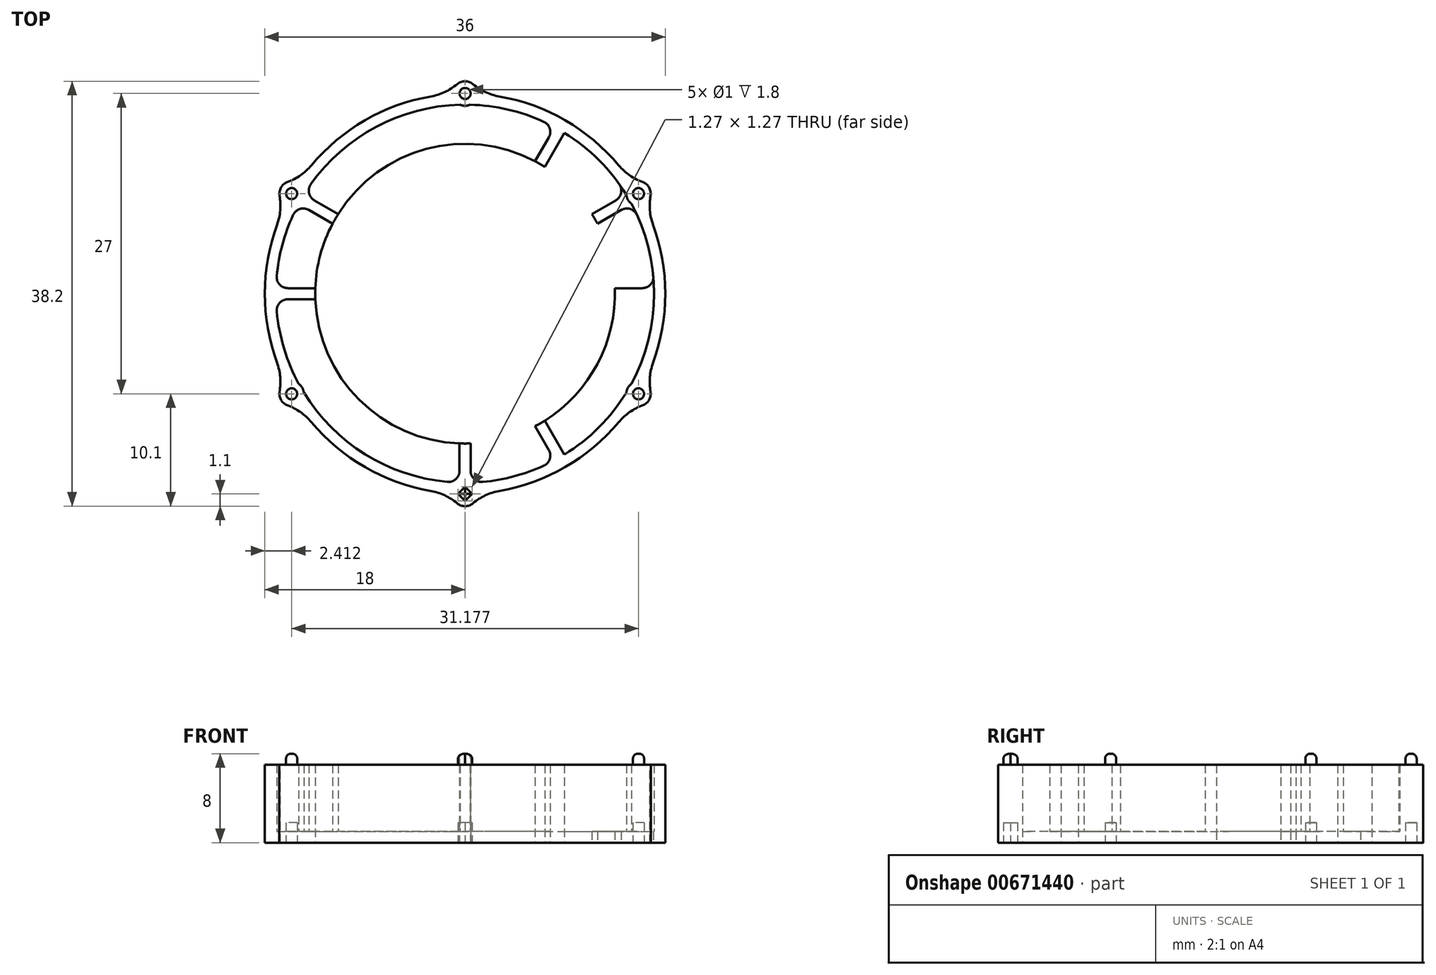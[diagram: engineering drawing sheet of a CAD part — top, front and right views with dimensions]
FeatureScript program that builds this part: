
annotation { "Feature Type Name" : "Feature", "Feature Type Description" : "" }
export const myFeature = defineFeature(function(context is Context, id is Id, definition is map)
    precondition{}
    {
        {
            var Q0;
            Q0=qCreatedBy(makeId("Top.planeOp"),FACE);
            var sketch = newSketch(context, id + "F0", { "sketchPlane" : qUnion([Q0])});
            skCircle(sketch, "E0", {"center": v(0, 0) * mm, "radius": 18 * mm});
            skCircle(sketch, "E1.0", {"center": v(0, 0) * mm, "radius": 17 * mm});
            skLineSegment(sketch, "E2.bottom", {"start": v(8.56, 15.83) * mm, "end": v(9.43, 15.33) * mm});
            skLineSegment(sketch, "E2.top", {"start": v(-9.43, -15.33) * mm, "end": v(-8.56, -15.83) * mm});
            skLineSegment(sketch, "E2.left", {"start": v(8.56, 15.83) * mm, "end": v(-9.43, -15.33) * mm});
            skLineSegment(sketch, "E2.right", {"start": v(9.43, 15.33) * mm, "end": v(-8.56, -15.83) * mm});
            skLineSegment(sketch, "E3.bottom", {"start": v(15.33, 9.43) * mm, "end": v(15.83, 8.56) * mm});
            skLineSegment(sketch, "E3.top", {"start": v(-15.83, -8.56) * mm, "end": v(-15.33, -9.43) * mm});
            skLineSegment(sketch, "E3.left", {"start": v(15.33, 9.43) * mm, "end": v(-15.83, -8.56) * mm});
            skLineSegment(sketch, "E3.right", {"start": v(15.83, 8.56) * mm, "end": v(-15.33, -9.43) * mm});
            skLineSegment(sketch, "E4", {"start": v(-38.35, 0) * mm, "end": v(39.17, 0) * mm, "construction": true});
            skLineSegment(sketch, "E5", {"start": v(0, 42.5) * mm, "end": v(0, -42.47) * mm, "construction": true});
            skLineSegment(sketch, "E6.bottom", {"start": v(-18, 0.5) * mm, "end": v(18, 0.5) * mm});
            skLineSegment(sketch, "E6.top", {"start": v(-18, -0.5) * mm, "end": v(18, -0.5) * mm});
            skLineSegment(sketch, "E6.left", {"start": v(-18, 0.5) * mm, "end": v(-18, -0.5) * mm});
            skLineSegment(sketch, "E6.right", {"start": v(18, 0.5) * mm, "end": v(18, -0.5) * mm});
            skLineSegment(sketch, "E7.bottom", {"start": v(-15.33, 9.43) * mm, "end": v(15.83, -8.56) * mm});
            skLineSegment(sketch, "E7.top", {"start": v(-15.83, 8.56) * mm, "end": v(15.33, -9.43) * mm});
            skLineSegment(sketch, "E7.left", {"start": v(-15.33, 9.43) * mm, "end": v(-15.83, 8.56) * mm});
            skLineSegment(sketch, "E7.right", {"start": v(15.83, -8.56) * mm, "end": v(15.33, -9.43) * mm});
            skLineSegment(sketch, "E8.bottom", {"start": v(-0.5, 18) * mm, "end": v(0.5, 18) * mm});
            skLineSegment(sketch, "E8.top", {"start": v(-0.5, -18) * mm, "end": v(0.5, -18) * mm});
            skLineSegment(sketch, "E8.left", {"start": v(-0.5, 18) * mm, "end": v(-0.5, -18) * mm});
            skLineSegment(sketch, "E8.right", {"start": v(0.5, 18) * mm, "end": v(0.5, -18) * mm});
            skLineSegment(sketch, "E9.bottom", {"start": v(-9.43, 15.33) * mm, "end": v(-8.56, 15.83) * mm});
            skLineSegment(sketch, "E9.top", {"start": v(8.56, -15.83) * mm, "end": v(9.43, -15.33) * mm});
            skLineSegment(sketch, "E9.left", {"start": v(-9.43, 15.33) * mm, "end": v(8.56, -15.83) * mm});
            skLineSegment(sketch, "E9.right", {"start": v(-8.56, 15.83) * mm, "end": v(9.43, -15.33) * mm});
            skCircle(sketch, "E10", {"center": v(0, 0) * mm, "radius": 13.47 * mm});
            skSolve(sketch);
        }
        {
            var Q0;
            Q0=qCreatedBy(makeId("Top.planeOp"),FACE);
            var sketch = newSketch(context, id + "F1", { "sketchPlane" : qUnion([Q0])});
            skCircle(sketch, "E11", {"center": v(0, 0) * mm, "radius": 18 * mm});
            skCircle(sketch, "E12", {"center": v(0, 0) * mm, "radius": 17 * mm});
            skSolve(sketch);
        }
        {
            var Q0;
            Q0=makeQuery(id+"F1.imprint","IMPRINT",FACE,{"disambiguationData":[TD([[makeQuery(id+"F1.imprint","IMPRINT",EDGE,{"derivedFrom":sQuery(id+"F1.wireOp",EDGE,"E11")}),1.0]])]});
            extrude(context, id + "F2", {"entities" : qUnion([Q0]), "depth" : 7 * mm, "offsetDistance" : 25 * mm});
        }
        {
            var Q0;
            {var subQ0=sQuery(id+"F0.wireOp",EDGE,"E7.bottom");var subQ1=sQuery(id+"F0.wireOp",EDGE,"E1.0");var subQ2=makeQuery(id+"F0.imprint","INTERSECT",VERTEX,{"disambiguationData":[OD(0.0)],"derivedFrom":[subQ1,subQ0]});Q0=makeQuery(id+"F0.imprint","IMPRINT",FACE,{"disambiguationData":[TD([[makeQuery(id+"F0.imprint","IMPRINT",EDGE,{"disambiguationData":[TD([[subQ2,-1.0]])],"derivedFrom":subQ1}),1.0]])]});}
            var Q1;
            {var subQ0=sQuery(id+"F0.wireOp",EDGE,"E2.right");var subQ1=sQuery(id+"F0.wireOp",EDGE,"E1.0");var subQ2=makeQuery(id+"F0.imprint","INTERSECT",VERTEX,{"disambiguationData":[OD(0.0)],"derivedFrom":[subQ1,subQ0]});Q1=makeQuery(id+"F0.imprint","IMPRINT",FACE,{"disambiguationData":[TD([[makeQuery(id+"F0.imprint","IMPRINT",EDGE,{"disambiguationData":[TD([[subQ2,-1.0]])],"derivedFrom":subQ1}),1.0]])]});}
            var Q2;
            {var subQ0=sQuery(id+"F0.wireOp",EDGE,"E8.left");var subQ1=sQuery(id+"F0.wireOp",EDGE,"E1.0");var subQ2=makeQuery(id+"F0.imprint","INTERSECT",VERTEX,{"disambiguationData":[OD(1.0)],"derivedFrom":[subQ1,subQ0]});Q2=makeQuery(id+"F0.imprint","IMPRINT",FACE,{"disambiguationData":[TD([[makeQuery(id+"F0.imprint","IMPRINT",EDGE,{"disambiguationData":[TD([[subQ2,-1.0]])],"derivedFrom":subQ1}),1.0]])]});}
            var Q3;
            {var subQ0=sQuery(id+"F0.wireOp",EDGE,"E9.left");var subQ1=sQuery(id+"F0.wireOp",EDGE,"E1.0");var subQ2=makeQuery(id+"F0.imprint","INTERSECT",VERTEX,{"disambiguationData":[OD(1.0)],"derivedFrom":[subQ1,subQ0]});Q3=makeQuery(id+"F0.imprint","IMPRINT",FACE,{"disambiguationData":[TD([[makeQuery(id+"F0.imprint","IMPRINT",EDGE,{"disambiguationData":[TD([[subQ2,-1.0]])],"derivedFrom":subQ1}),1.0]])]});}
            var Q4;
            {var subQ0=sQuery(id+"F0.wireOp",EDGE,"E6.bottom");var subQ1=sQuery(id+"F0.wireOp",EDGE,"E1.0");var subQ2=makeQuery(id+"F0.imprint","INTERSECT",VERTEX,{"disambiguationData":[OD(1.0)],"derivedFrom":[subQ1,subQ0]});Q4=makeQuery(id+"F0.imprint","IMPRINT",FACE,{"disambiguationData":[TD([[makeQuery(id+"F0.imprint","IMPRINT",EDGE,{"disambiguationData":[TD([[subQ2,-1.0]])],"derivedFrom":subQ1}),1.0]])]});}
            extrude(context, id + "F3", {"entities" : qUnion([Q0, Q1, Q2, Q3, Q4]), "operationType" : NewBodyOperationType.ADD, "depth" : 7 * mm, "offsetDistance" : 25 * mm});
        }
        {
            var Q0;
            Q0=makeQuery(id+"F1.imprint","IMPRINT",FACE,{"disambiguationData":[TD([[makeQuery(id+"F1.imprint","IMPRINT",EDGE,{"derivedFrom":sQuery(id+"F1.wireOp",EDGE,"E11")}),1.0]])]});
            var Q1;
            Q1=makeQuery(id+"F1.imprint","IMPRINT",FACE,{"disambiguationData":[TD([[makeQuery(id+"F1.imprint","IMPRINT",EDGE,{"derivedFrom":sQuery(id+"F1.wireOp",EDGE,"E12")}),1.0]])]});
            extrude(context, id + "F4", {"entities" : qUnion([Q0, Q1]), "operationType" : NewBodyOperationType.ADD, "depth" : 1 * mm, "offsetDistance" : 25 * mm});
        }
        {
            var Q0;
            Q0=qCreatedBy(makeId("Top.planeOp"),FACE);
            var sketch = newSketch(context, id + "F5", { "sketchPlane" : qUnion([Q0])});
            skCircle(sketch, "E13", {"center": v(0, 0) * mm, "radius": 18 * mm});
            skLineSegment(sketch, "E14", {"start": v(0, 18) * mm, "end": v(0, -18) * mm, "construction": true});
            skLineSegment(sketch, "E15", {"start": v(15.59, 9) * mm, "end": v(0, 0) * mm, "construction": true});
            skLineSegment(sketch, "E16", {"start": v(9, 15.59) * mm, "end": v(0, 0) * mm, "construction": true});
            skLineSegment(sketch, "E17", {"start": v(0, 0) * mm, "end": v(18, 0) * mm, "construction": true});
            skLineSegment(sketch, "E18", {"start": v(0, 0) * mm, "end": v(15.59, -9) * mm, "construction": true});
            skLineSegment(sketch, "E19", {"start": v(0, 0) * mm, "end": v(9, -15.59) * mm, "construction": true});
            skLineSegment(sketch, "E20", {"start": v(0, 0) * mm, "end": v(-9, 15.59) * mm, "construction": true});
            skLineSegment(sketch, "E21", {"start": v(0, 0) * mm, "end": v(-15.59, 9) * mm, "construction": true});
            skLineSegment(sketch, "E22", {"start": v(0, 0) * mm, "end": v(-18, 0) * mm, "construction": true});
            skLineSegment(sketch, "E23", {"start": v(0, 0) * mm, "end": v(-15.59, -9) * mm, "construction": true});
            skLineSegment(sketch, "E24", {"start": v(0, 0) * mm, "end": v(-9, -15.59) * mm, "construction": true});
            skCircle(sketch, "E25", {"center": v(0, 18) * mm, "radius": 1.1 * mm});
            skCircle(sketch, "E26", {"center": v(15.59, 9) * mm, "radius": 1.1 * mm});
            skCircle(sketch, "E27", {"center": v(15.59, -9) * mm, "radius": 1.1 * mm});
            skCircle(sketch, "E28", {"center": v(0, -18) * mm, "radius": 1.1 * mm});
            skCircle(sketch, "E29", {"center": v(-15.59, -9) * mm, "radius": 1.1 * mm});
            skCircle(sketch, "E30", {"center": v(-15.59, 9) * mm, "radius": 1.1 * mm});
            skCircle(sketch, "E31", {"center": v(-15.59, 9) * mm, "radius": 0.5 * mm});
            skCircle(sketch, "E32", {"center": v(0, 18) * mm, "radius": 0.5 * mm});
            skCircle(sketch, "E33", {"center": v(15.59, 9) * mm, "radius": 0.5 * mm});
            skCircle(sketch, "E34", {"center": v(15.59, -9) * mm, "radius": 0.5 * mm});
            skCircle(sketch, "E35", {"center": v(-15.59, -9) * mm, "radius": 0.5 * mm});
            skLineSegment(sketch, "E36.bottom", {"start": v(0.64, -18) * mm, "end": v(0, -18.64) * mm});
            skLineSegment(sketch, "E36.top", {"start": v(0, -17.36) * mm, "end": v(-0.64, -18) * mm});
            skLineSegment(sketch, "E36.left", {"start": v(0.64, -18) * mm, "end": v(0, -17.36) * mm});
            skLineSegment(sketch, "E36.right", {"start": v(0, -18.64) * mm, "end": v(-0.64, -18) * mm});
            skSolve(sketch);
        }
        {
            var Q0;
            {var subQ0=sQuery(id+"F5.wireOp",EDGE,"E30");var subQ1=sQuery(id+"F5.wireOp",EDGE,"E13");var subQ2=makeQuery(id+"F5.imprint","INTERSECT",VERTEX,{"disambiguationData":[OD(0.0)],"derivedFrom":[subQ1,subQ0]});Q0=makeQuery(id+"F5.imprint","IMPRINT",FACE,{"disambiguationData":[TD([[makeQuery(id+"F5.imprint","IMPRINT",EDGE,{"disambiguationData":[TD([[subQ2,-1.0]])],"derivedFrom":subQ1}),1.0]])]});}
            var Q1;
            {var subQ0=sQuery(id+"F5.wireOp",EDGE,"E30");var subQ1=sQuery(id+"F5.wireOp",EDGE,"E13");var subQ2=makeQuery(id+"F5.imprint","INTERSECT",VERTEX,{"disambiguationData":[OD(0.0)],"derivedFrom":[subQ1,subQ0]});Q1=makeQuery(id+"F5.imprint","IMPRINT",FACE,{"disambiguationData":[TD([[makeQuery(id+"F5.imprint","IMPRINT",EDGE,{"disambiguationData":[TD([[subQ2,-1.0]])],"derivedFrom":subQ1}),-1.0]])]});}
            var Q2;
            {var subQ0=sQuery(id+"F5.wireOp",EDGE,"E25");var subQ1=sQuery(id+"F5.wireOp",EDGE,"E13");var subQ2=makeQuery(id+"F5.imprint","INTERSECT",VERTEX,{"disambiguationData":[OD(0.0)],"derivedFrom":[subQ1,subQ0]});Q2=makeQuery(id+"F5.imprint","IMPRINT",FACE,{"disambiguationData":[TD([[makeQuery(id+"F5.imprint","IMPRINT",EDGE,{"disambiguationData":[TD([[subQ2,-1.0]])],"derivedFrom":subQ1}),1.0]])]});}
            var Q3;
            {var subQ0=sQuery(id+"F5.wireOp",EDGE,"E25");var subQ1=sQuery(id+"F5.wireOp",EDGE,"E13");var subQ2=makeQuery(id+"F5.imprint","INTERSECT",VERTEX,{"disambiguationData":[OD(0.0)],"derivedFrom":[subQ1,subQ0]});Q3=makeQuery(id+"F5.imprint","IMPRINT",FACE,{"disambiguationData":[TD([[makeQuery(id+"F5.imprint","IMPRINT",EDGE,{"disambiguationData":[TD([[subQ2,-1.0]])],"derivedFrom":subQ1}),-1.0]])]});}
            var Q4;
            {var subQ0=sQuery(id+"F5.wireOp",EDGE,"E26");var subQ1=sQuery(id+"F5.wireOp",EDGE,"E13");var subQ2=makeQuery(id+"F5.imprint","INTERSECT",VERTEX,{"disambiguationData":[OD(0.0)],"derivedFrom":[subQ1,subQ0]});Q4=makeQuery(id+"F5.imprint","IMPRINT",FACE,{"disambiguationData":[TD([[makeQuery(id+"F5.imprint","IMPRINT",EDGE,{"disambiguationData":[TD([[subQ2,-1.0]])],"derivedFrom":subQ1}),-1.0]])]});}
            var Q5;
            {var subQ0=sQuery(id+"F5.wireOp",EDGE,"E26");var subQ1=sQuery(id+"F5.wireOp",EDGE,"E13");var subQ2=makeQuery(id+"F5.imprint","INTERSECT",VERTEX,{"disambiguationData":[OD(0.0)],"derivedFrom":[subQ1,subQ0]});Q5=makeQuery(id+"F5.imprint","IMPRINT",FACE,{"disambiguationData":[TD([[makeQuery(id+"F5.imprint","IMPRINT",EDGE,{"disambiguationData":[TD([[subQ2,-1.0]])],"derivedFrom":subQ1}),1.0]])]});}
            var Q6;
            {var subQ0=sQuery(id+"F5.wireOp",EDGE,"E29");var subQ1=sQuery(id+"F5.wireOp",EDGE,"E13");var subQ2=makeQuery(id+"F5.imprint","INTERSECT",VERTEX,{"disambiguationData":[OD(0.0)],"derivedFrom":[subQ1,subQ0]});Q6=makeQuery(id+"F5.imprint","IMPRINT",FACE,{"disambiguationData":[TD([[makeQuery(id+"F5.imprint","IMPRINT",EDGE,{"disambiguationData":[TD([[subQ2,-1.0]])],"derivedFrom":subQ1}),1.0]])]});}
            var Q7;
            {var subQ0=sQuery(id+"F5.wireOp",EDGE,"E29");var subQ1=sQuery(id+"F5.wireOp",EDGE,"E13");var subQ2=makeQuery(id+"F5.imprint","INTERSECT",VERTEX,{"disambiguationData":[OD(0.0)],"derivedFrom":[subQ1,subQ0]});Q7=makeQuery(id+"F5.imprint","IMPRINT",FACE,{"disambiguationData":[TD([[makeQuery(id+"F5.imprint","IMPRINT",EDGE,{"disambiguationData":[TD([[subQ2,-1.0]])],"derivedFrom":subQ1}),-1.0]])]});}
            var Q8;
            {var subQ3=sQuery(id+"F5.wireOp",EDGE,"E13");var subQ5=sQuery(id+"F5.wireOp",EDGE,"E28");var subQ6=makeQuery(id+"F5.imprint","INTERSECT",VERTEX,{"disambiguationData":[OD(0.0)],"derivedFrom":[subQ3,subQ5]});Q8=makeQuery(id+"F5.imprint","IMPRINT",FACE,{"disambiguationData":[TD([[makeQuery(id+"F5.imprint","IMPRINT",EDGE,{"disambiguationData":[TD([[subQ6,-1.0]])],"derivedFrom":subQ3}),1.0]])]});}
            var Q9;
            {var subQ6=sQuery(id+"F5.wireOp",EDGE,"E36.bottom");Q9=makeQuery(id+"F5.imprint","IMPRINT",FACE,{"disambiguationData":[TD([[makeQuery(id+"F5.imprint","IMPRINT",EDGE,{"derivedFrom":subQ6}),1.0]])]});}
            var Q10;
            {var subQ0=sQuery(id+"F5.wireOp",EDGE,"E27");var subQ1=sQuery(id+"F5.wireOp",EDGE,"E13");var subQ2=makeQuery(id+"F5.imprint","INTERSECT",VERTEX,{"disambiguationData":[OD(0.0)],"derivedFrom":[subQ1,subQ0]});Q10=makeQuery(id+"F5.imprint","IMPRINT",FACE,{"disambiguationData":[TD([[makeQuery(id+"F5.imprint","IMPRINT",EDGE,{"disambiguationData":[TD([[subQ2,-1.0]])],"derivedFrom":subQ1}),-1.0]])]});}
            var Q11;
            {var subQ0=sQuery(id+"F5.wireOp",EDGE,"E27");var subQ1=sQuery(id+"F5.wireOp",EDGE,"E13");var subQ2=makeQuery(id+"F5.imprint","INTERSECT",VERTEX,{"disambiguationData":[OD(0.0)],"derivedFrom":[subQ1,subQ0]});Q11=makeQuery(id+"F5.imprint","IMPRINT",FACE,{"disambiguationData":[TD([[makeQuery(id+"F5.imprint","IMPRINT",EDGE,{"disambiguationData":[TD([[subQ2,-1.0]])],"derivedFrom":subQ1}),1.0]])]});}
            var Q12;
            {var subQ0=sQuery(id+"F5.wireOp",EDGE,"E31");var subQ1=sQuery(id+"F5.wireOp",EDGE,"E13");var subQ2=makeQuery(id+"F5.imprint","INTERSECT",VERTEX,{"disambiguationData":[OD(0.0)],"derivedFrom":[subQ1,subQ0]});Q12=makeQuery(id+"F5.imprint","IMPRINT",FACE,{"disambiguationData":[TD([[makeQuery(id+"F5.imprint","IMPRINT",EDGE,{"disambiguationData":[TD([[subQ2,-1.0]])],"derivedFrom":subQ1}),1.0]])]});}
            var Q13;
            {var subQ0=sQuery(id+"F5.wireOp",EDGE,"E31");var subQ1=sQuery(id+"F5.wireOp",EDGE,"E13");var subQ2=makeQuery(id+"F5.imprint","INTERSECT",VERTEX,{"disambiguationData":[OD(0.0)],"derivedFrom":[subQ1,subQ0]});Q13=makeQuery(id+"F5.imprint","IMPRINT",FACE,{"disambiguationData":[TD([[makeQuery(id+"F5.imprint","IMPRINT",EDGE,{"disambiguationData":[TD([[subQ2,-1.0]])],"derivedFrom":subQ1}),-1.0]])]});}
            var Q14;
            {var subQ0=sQuery(id+"F5.wireOp",EDGE,"E32");var subQ1=sQuery(id+"F5.wireOp",EDGE,"E13");var subQ2=makeQuery(id+"F5.imprint","INTERSECT",VERTEX,{"disambiguationData":[OD(0.0)],"derivedFrom":[subQ1,subQ0]});Q14=makeQuery(id+"F5.imprint","IMPRINT",FACE,{"disambiguationData":[TD([[makeQuery(id+"F5.imprint","IMPRINT",EDGE,{"disambiguationData":[TD([[subQ2,-1.0]])],"derivedFrom":subQ1}),-1.0]])]});}
            var Q15;
            {var subQ0=sQuery(id+"F5.wireOp",EDGE,"E32");var subQ1=sQuery(id+"F5.wireOp",EDGE,"E13");var subQ2=makeQuery(id+"F5.imprint","INTERSECT",VERTEX,{"disambiguationData":[OD(0.0)],"derivedFrom":[subQ1,subQ0]});Q15=makeQuery(id+"F5.imprint","IMPRINT",FACE,{"disambiguationData":[TD([[makeQuery(id+"F5.imprint","IMPRINT",EDGE,{"disambiguationData":[TD([[subQ2,-1.0]])],"derivedFrom":subQ1}),1.0]])]});}
            var Q16;
            {var subQ0=sQuery(id+"F5.wireOp",EDGE,"E33");var subQ1=sQuery(id+"F5.wireOp",EDGE,"E13");var subQ2=makeQuery(id+"F5.imprint","INTERSECT",VERTEX,{"disambiguationData":[OD(0.0)],"derivedFrom":[subQ1,subQ0]});Q16=makeQuery(id+"F5.imprint","IMPRINT",FACE,{"disambiguationData":[TD([[makeQuery(id+"F5.imprint","IMPRINT",EDGE,{"disambiguationData":[TD([[subQ2,-1.0]])],"derivedFrom":subQ1}),-1.0]])]});}
            var Q17;
            {var subQ0=sQuery(id+"F5.wireOp",EDGE,"E33");var subQ1=sQuery(id+"F5.wireOp",EDGE,"E13");var subQ2=makeQuery(id+"F5.imprint","INTERSECT",VERTEX,{"disambiguationData":[OD(0.0)],"derivedFrom":[subQ1,subQ0]});Q17=makeQuery(id+"F5.imprint","IMPRINT",FACE,{"disambiguationData":[TD([[makeQuery(id+"F5.imprint","IMPRINT",EDGE,{"disambiguationData":[TD([[subQ2,-1.0]])],"derivedFrom":subQ1}),1.0]])]});}
            var Q18;
            {var subQ0=sQuery(id+"F5.wireOp",EDGE,"E34");var subQ1=sQuery(id+"F5.wireOp",EDGE,"E13");var subQ2=makeQuery(id+"F5.imprint","INTERSECT",VERTEX,{"disambiguationData":[OD(0.0)],"derivedFrom":[subQ1,subQ0]});Q18=makeQuery(id+"F5.imprint","IMPRINT",FACE,{"disambiguationData":[TD([[makeQuery(id+"F5.imprint","IMPRINT",EDGE,{"disambiguationData":[TD([[subQ2,-1.0]])],"derivedFrom":subQ1}),-1.0]])]});}
            var Q19;
            {var subQ0=sQuery(id+"F5.wireOp",EDGE,"E34");var subQ1=sQuery(id+"F5.wireOp",EDGE,"E13");var subQ2=makeQuery(id+"F5.imprint","INTERSECT",VERTEX,{"disambiguationData":[OD(0.0)],"derivedFrom":[subQ1,subQ0]});Q19=makeQuery(id+"F5.imprint","IMPRINT",FACE,{"disambiguationData":[TD([[makeQuery(id+"F5.imprint","IMPRINT",EDGE,{"disambiguationData":[TD([[subQ2,-1.0]])],"derivedFrom":subQ1}),1.0]])]});}
            var Q20;
            {var subQ1=sQuery(id+"F5.wireOp",EDGE,"E36.bottom");Q20=makeQuery(id+"F5.imprint","IMPRINT",FACE,{"disambiguationData":[TD([[makeQuery(id+"F5.imprint","IMPRINT",EDGE,{"derivedFrom":subQ1}),-1.0]])]});}
            var Q21;
            {var subQ0=sQuery(id+"F5.wireOp",EDGE,"E35");var subQ1=sQuery(id+"F5.wireOp",EDGE,"E13");var subQ2=makeQuery(id+"F5.imprint","INTERSECT",VERTEX,{"disambiguationData":[OD(0.0)],"derivedFrom":[subQ1,subQ0]});Q21=makeQuery(id+"F5.imprint","IMPRINT",FACE,{"disambiguationData":[TD([[makeQuery(id+"F5.imprint","IMPRINT",EDGE,{"disambiguationData":[TD([[subQ2,-1.0]])],"derivedFrom":subQ1}),-1.0]])]});}
            var Q22;
            {var subQ0=sQuery(id+"F5.wireOp",EDGE,"E35");var subQ1=sQuery(id+"F5.wireOp",EDGE,"E13");var subQ2=makeQuery(id+"F5.imprint","INTERSECT",VERTEX,{"disambiguationData":[OD(0.0)],"derivedFrom":[subQ1,subQ0]});Q22=makeQuery(id+"F5.imprint","IMPRINT",FACE,{"disambiguationData":[TD([[makeQuery(id+"F5.imprint","IMPRINT",EDGE,{"disambiguationData":[TD([[subQ2,-1.0]])],"derivedFrom":subQ1}),1.0]])]});}
            var Q23;
            {var subQ0=sQuery(id+"F5.wireOp",EDGE,"E36.top");var subQ1=sQuery(id+"F5.wireOp",EDGE,"E13");var subQ2=makeQuery(id+"F5.imprint","INTERSECT",VERTEX,{"derivedFrom":[subQ1,subQ0]});Q23=makeQuery(id+"F5.imprint","IMPRINT",FACE,{"disambiguationData":[TD([[makeQuery(id+"F5.imprint","IMPRINT",EDGE,{"disambiguationData":[TD([[subQ2,-1.0]])],"derivedFrom":subQ1}),1.0]])]});}
            extrude(context, id + "F6", {"entities" : qUnion([Q0, Q1, Q2, Q3, Q4, Q5, Q6, Q7, Q8, Q9, Q10, Q11, Q12, Q13, Q14, Q15, Q16, Q17, Q18, Q19, Q20, Q21, Q22, Q23]), "operationType" : NewBodyOperationType.ADD, "depth" : 7 * mm, "offsetDistance" : 25 * mm});
        }
        {
            var Q0;
            {var subQ0=sQuery(id+"F0.wireOp",EDGE,"E8.right");var subQ1=sQuery(id+"F0.wireOp",EDGE,"E1.0");Q0=makeQuery(id+"F3.opExtrude","SWEPT_EDGE",EDGE,{"disambiguationData":[OSD([subQ1,subQ0]),TDD([makeQuery(id+"F0.imprint","INTERSECT",VERTEX,{"disambiguationData":[OD(1.0)],"derivedFrom":[subQ1,subQ0]})])]});}
            var Q1;
            {var subQ0=sQuery(id+"F0.wireOp",EDGE,"E2.left");var subQ1=sQuery(id+"F0.wireOp",EDGE,"E1.0");Q1=makeQuery(id+"F3.opExtrude","SWEPT_EDGE",EDGE,{"disambiguationData":[OSD([subQ1,subQ0]),TDD([makeQuery(id+"F0.imprint","INTERSECT",VERTEX,{"disambiguationData":[OD(1.0)],"derivedFrom":[subQ1,subQ0]})])]});}
            var Q2;
            {var subQ0=sQuery(id+"F0.wireOp",EDGE,"E3.left");var subQ1=sQuery(id+"F0.wireOp",EDGE,"E1.0");Q2=makeQuery(id+"F3.opExtrude","SWEPT_EDGE",EDGE,{"disambiguationData":[OSD([subQ1,subQ0]),TDD([makeQuery(id+"F0.imprint","INTERSECT",VERTEX,{"disambiguationData":[OD(1.0)],"derivedFrom":[subQ1,subQ0]})])]});}
            var Q3;
            {var subQ0=sQuery(id+"F0.wireOp",EDGE,"E6.bottom");var subQ1=sQuery(id+"F0.wireOp",EDGE,"E1.0");Q3=makeQuery(id+"F3.opExtrude","SWEPT_EDGE",EDGE,{"disambiguationData":[OSD([subQ1,subQ0]),TDD([makeQuery(id+"F0.imprint","INTERSECT",VERTEX,{"disambiguationData":[OD(1.0)],"derivedFrom":[subQ1,subQ0]})])]});}
            var Q4;
            {var subQ0=sQuery(id+"F0.wireOp",EDGE,"E9.right");var subQ1=sQuery(id+"F0.wireOp",EDGE,"E1.0");Q4=makeQuery(id+"F3.opExtrude","SWEPT_EDGE",EDGE,{"disambiguationData":[OSD([subQ1,subQ0]),TDD([makeQuery(id+"F0.imprint","INTERSECT",VERTEX,{"disambiguationData":[OD(1.0)],"derivedFrom":[subQ1,subQ0]})])]});}
            var Q5;
            {var subQ0=sQuery(id+"F0.wireOp",EDGE,"E7.bottom");var subQ1=sQuery(id+"F0.wireOp",EDGE,"E1.0");Q5=makeQuery(id+"F3.opExtrude","SWEPT_EDGE",EDGE,{"disambiguationData":[OSD([subQ1,subQ0]),TDD([makeQuery(id+"F0.imprint","INTERSECT",VERTEX,{"disambiguationData":[OD(1.0)],"derivedFrom":[subQ1,subQ0]})])]});}
            var Q6;
            {var subQ0=sQuery(id+"F0.wireOp",EDGE,"E8.left");var subQ1=sQuery(id+"F0.wireOp",EDGE,"E1.0");Q6=makeQuery(id+"F3.opExtrude","SWEPT_EDGE",EDGE,{"disambiguationData":[OSD([subQ1,subQ0]),TDD([makeQuery(id+"F0.imprint","INTERSECT",VERTEX,{"disambiguationData":[OD(0.0)],"derivedFrom":[subQ1,subQ0]})])]});}
            var Q7;
            {var subQ0=sQuery(id+"F0.wireOp",EDGE,"E2.left");var subQ1=sQuery(id+"F0.wireOp",EDGE,"E1.0");Q7=makeQuery(id+"F3.opExtrude","SWEPT_EDGE",EDGE,{"disambiguationData":[OSD([subQ1,subQ0]),TDD([makeQuery(id+"F0.imprint","INTERSECT",VERTEX,{"disambiguationData":[OD(0.0)],"derivedFrom":[subQ1,subQ0]})])]});}
            var Q8;
            {var subQ0=sQuery(id+"F0.wireOp",EDGE,"E3.left");var subQ1=sQuery(id+"F0.wireOp",EDGE,"E1.0");Q8=makeQuery(id+"F3.opExtrude","SWEPT_EDGE",EDGE,{"disambiguationData":[OSD([subQ1,subQ0]),TDD([makeQuery(id+"F0.imprint","INTERSECT",VERTEX,{"disambiguationData":[OD(0.0)],"derivedFrom":[subQ1,subQ0]})])]});}
            var Q9;
            {var subQ0=sQuery(id+"F0.wireOp",EDGE,"E6.top");var subQ1=sQuery(id+"F0.wireOp",EDGE,"E1.0");Q9=makeQuery(id+"F3.opExtrude","SWEPT_EDGE",EDGE,{"disambiguationData":[OSD([subQ1,subQ0]),TDD([makeQuery(id+"F0.imprint","INTERSECT",VERTEX,{"disambiguationData":[OD(1.0)],"derivedFrom":[subQ1,subQ0]})])]});}
            var Q10;
            {var subQ0=sQuery(id+"F0.wireOp",EDGE,"E7.top");var subQ1=sQuery(id+"F0.wireOp",EDGE,"E1.0");Q10=makeQuery(id+"F3.opExtrude","SWEPT_EDGE",EDGE,{"disambiguationData":[OSD([subQ1,subQ0]),TDD([makeQuery(id+"F0.imprint","INTERSECT",VERTEX,{"disambiguationData":[OD(0.0)],"derivedFrom":[subQ1,subQ0]})])]});}
            var Q11;
            {var subQ0=sQuery(id+"F0.wireOp",EDGE,"E6.top");var subQ1=sQuery(id+"F0.wireOp",EDGE,"E1.0");Q11=makeQuery(id+"F3.opExtrude","SWEPT_EDGE",EDGE,{"disambiguationData":[OSD([subQ1,subQ0]),TDD([makeQuery(id+"F0.imprint","INTERSECT",VERTEX,{"disambiguationData":[OD(0.0)],"derivedFrom":[subQ1,subQ0]})])]});}
            var Q12;
            {var subQ0=sQuery(id+"F0.wireOp",EDGE,"E9.left");var subQ1=sQuery(id+"F0.wireOp",EDGE,"E1.0");Q12=makeQuery(id+"F3.opExtrude","SWEPT_EDGE",EDGE,{"disambiguationData":[OSD([subQ1,subQ0]),TDD([makeQuery(id+"F0.imprint","INTERSECT",VERTEX,{"disambiguationData":[OD(0.0)],"derivedFrom":[subQ1,subQ0]})])]});}
            var Q13;
            {var subQ0=sQuery(id+"F0.wireOp",EDGE,"E8.right");var subQ1=sQuery(id+"F0.wireOp",EDGE,"E1.0");Q13=makeQuery(id+"F3.opExtrude","SWEPT_EDGE",EDGE,{"disambiguationData":[OSD([subQ1,subQ0]),TDD([makeQuery(id+"F0.imprint","INTERSECT",VERTEX,{"disambiguationData":[OD(0.0)],"derivedFrom":[subQ1,subQ0]})])]});}
            var Q14;
            {var subQ0=sQuery(id+"F0.wireOp",EDGE,"E7.bottom");var subQ1=sQuery(id+"F0.wireOp",EDGE,"E1.0");Q14=makeQuery(id+"F3.opExtrude","SWEPT_EDGE",EDGE,{"disambiguationData":[OSD([subQ1,subQ0]),TDD([makeQuery(id+"F0.imprint","INTERSECT",VERTEX,{"disambiguationData":[OD(0.0)],"derivedFrom":[subQ1,subQ0]})])]});}
            var Q15;
            {var subQ0=sQuery(id+"F0.wireOp",EDGE,"E9.right");var subQ1=sQuery(id+"F0.wireOp",EDGE,"E1.0");Q15=makeQuery(id+"F3.opExtrude","SWEPT_EDGE",EDGE,{"disambiguationData":[OSD([subQ1,subQ0]),TDD([makeQuery(id+"F0.imprint","INTERSECT",VERTEX,{"disambiguationData":[OD(0.0)],"derivedFrom":[subQ1,subQ0]})])]});}
            var Q16;
            {var subQ0=sQuery(id+"F0.wireOp",EDGE,"E3.right");var subQ1=sQuery(id+"F0.wireOp",EDGE,"E1.0");Q16=makeQuery(id+"F3.opExtrude","SWEPT_EDGE",EDGE,{"disambiguationData":[OSD([subQ1,subQ0]),TDD([makeQuery(id+"F0.imprint","INTERSECT",VERTEX,{"disambiguationData":[OD(1.0)],"derivedFrom":[subQ1,subQ0]})])]});}
            var Q17;
            {var subQ0=sQuery(id+"F0.wireOp",EDGE,"E2.right");var subQ1=sQuery(id+"F0.wireOp",EDGE,"E1.0");Q17=makeQuery(id+"F3.opExtrude","SWEPT_EDGE",EDGE,{"disambiguationData":[OSD([subQ1,subQ0]),TDD([makeQuery(id+"F0.imprint","INTERSECT",VERTEX,{"disambiguationData":[OD(1.0)],"derivedFrom":[subQ1,subQ0]})])]});}
            var Q18;
            {var subQ0=sQuery(id+"F0.wireOp",EDGE,"E3.right");var subQ1=sQuery(id+"F0.wireOp",EDGE,"E1.0");Q18=makeQuery(id+"F3.opExtrude","SWEPT_EDGE",EDGE,{"disambiguationData":[OSD([subQ1,subQ0]),TDD([makeQuery(id+"F0.imprint","INTERSECT",VERTEX,{"disambiguationData":[OD(0.0)],"derivedFrom":[subQ1,subQ0]})])]});}
            var Q19;
            {var subQ0=sQuery(id+"F0.wireOp",EDGE,"E2.right");var subQ1=sQuery(id+"F0.wireOp",EDGE,"E1.0");Q19=makeQuery(id+"F3.opExtrude","SWEPT_EDGE",EDGE,{"disambiguationData":[OSD([subQ1,subQ0]),TDD([makeQuery(id+"F0.imprint","INTERSECT",VERTEX,{"disambiguationData":[OD(0.0)],"derivedFrom":[subQ1,subQ0]})])]});}
            var Q20;
            {var subQ0=sQuery(id+"F0.wireOp",EDGE,"E8.left");var subQ1=sQuery(id+"F0.wireOp",EDGE,"E1.0");Q20=makeQuery(id+"F3.opExtrude","SWEPT_EDGE",EDGE,{"disambiguationData":[OSD([subQ1,subQ0]),TDD([makeQuery(id+"F0.imprint","INTERSECT",VERTEX,{"disambiguationData":[OD(1.0)],"derivedFrom":[subQ1,subQ0]})])]});}
            var Q21;
            {var subQ0=sQuery(id+"F0.wireOp",EDGE,"E9.left");var subQ1=sQuery(id+"F0.wireOp",EDGE,"E1.0");Q21=makeQuery(id+"F3.opExtrude","SWEPT_EDGE",EDGE,{"disambiguationData":[OSD([subQ1,subQ0]),TDD([makeQuery(id+"F0.imprint","INTERSECT",VERTEX,{"disambiguationData":[OD(1.0)],"derivedFrom":[subQ1,subQ0]})])]});}
            var Q22;
            {var subQ0=sQuery(id+"F0.wireOp",EDGE,"E7.top");var subQ1=sQuery(id+"F0.wireOp",EDGE,"E1.0");Q22=makeQuery(id+"F3.opExtrude","SWEPT_EDGE",EDGE,{"disambiguationData":[OSD([subQ1,subQ0]),TDD([makeQuery(id+"F0.imprint","INTERSECT",VERTEX,{"disambiguationData":[OD(1.0)],"derivedFrom":[subQ1,subQ0]})])]});}
            var Q23;
            {var subQ0=sQuery(id+"F0.wireOp",EDGE,"E6.bottom");var subQ1=sQuery(id+"F0.wireOp",EDGE,"E1.0");Q23=makeQuery(id+"F3.opExtrude","SWEPT_EDGE",EDGE,{"disambiguationData":[OSD([subQ1,subQ0]),TDD([makeQuery(id+"F0.imprint","INTERSECT",VERTEX,{"disambiguationData":[OD(0.0)],"derivedFrom":[subQ1,subQ0]})])]});}
            fillet(context, id + "F7", {"entities" : qUnion([Q0, Q1, Q2, Q3, Q4, Q5, Q6, Q7, Q8, Q9, Q10, Q11, Q12, Q13, Q14, Q15, Q16, Q17, Q18, Q19, Q20, Q21, Q22, Q23]), "radius" : 1 * mm, "tangentPropagation" : true, "allowEdgeOverflow" : false});
        }
        {
            var Q0;
            Q0=makeQuery(id+"F6.boolean.opBoolean","INTERSECT",EDGE,{"disambiguationData":[OD(0.0)],"derivedFrom":[makeQuery(id+"F2.opExtrude","SWEPT_FACE",FACE,{"disambiguationData":[OSD([sQuery(id+"F1.wireOp",EDGE,"E11")])]}),makeQuery(id+"F6.opExtrude","SWEPT_FACE",FACE,{"disambiguationData":[OSD([sQuery(id+"F5.wireOp",EDGE,"E30")])]})]});
            var Q1;
            Q1=makeQuery(id+"F6.boolean.opBoolean","INTERSECT",EDGE,{"disambiguationData":[OD(1.0)],"derivedFrom":[makeQuery(id+"F2.opExtrude","SWEPT_FACE",FACE,{"disambiguationData":[OSD([sQuery(id+"F1.wireOp",EDGE,"E11")])]}),makeQuery(id+"F6.opExtrude","SWEPT_FACE",FACE,{"disambiguationData":[OSD([sQuery(id+"F5.wireOp",EDGE,"E30")])]})]});
            var Q2;
            Q2=makeQuery(id+"F6.boolean.opBoolean","INTERSECT",EDGE,{"disambiguationData":[OD(1.0)],"derivedFrom":[makeQuery(id+"F2.opExtrude","SWEPT_FACE",FACE,{"disambiguationData":[OSD([sQuery(id+"F1.wireOp",EDGE,"E11")])]}),makeQuery(id+"F6.opExtrude","SWEPT_FACE",FACE,{"disambiguationData":[OSD([sQuery(id+"F5.wireOp",EDGE,"E25")])]})]});
            var Q3;
            Q3=makeQuery(id+"F6.boolean.opBoolean","INTERSECT",EDGE,{"disambiguationData":[OD(1.0)],"derivedFrom":[makeQuery(id+"F2.opExtrude","SWEPT_FACE",FACE,{"disambiguationData":[OSD([sQuery(id+"F1.wireOp",EDGE,"E11")])]}),makeQuery(id+"F6.opExtrude","SWEPT_FACE",FACE,{"disambiguationData":[OSD([sQuery(id+"F5.wireOp",EDGE,"E29")])]})]});
            var Q4;
            Q4=makeQuery(id+"F6.boolean.opBoolean","INTERSECT",EDGE,{"disambiguationData":[OD(0.0)],"derivedFrom":[makeQuery(id+"F2.opExtrude","SWEPT_FACE",FACE,{"disambiguationData":[OSD([sQuery(id+"F1.wireOp",EDGE,"E11")])]}),makeQuery(id+"F6.opExtrude","SWEPT_FACE",FACE,{"disambiguationData":[OSD([sQuery(id+"F5.wireOp",EDGE,"E29")])]})]});
            var Q5;
            Q5=makeQuery(id+"F6.boolean.opBoolean","INTERSECT",EDGE,{"disambiguationData":[OD(1.0)],"derivedFrom":[makeQuery(id+"F2.opExtrude","SWEPT_FACE",FACE,{"disambiguationData":[OSD([sQuery(id+"F1.wireOp",EDGE,"E11")])]}),makeQuery(id+"F6.opExtrude","SWEPT_FACE",FACE,{"disambiguationData":[OSD([sQuery(id+"F5.wireOp",EDGE,"E28")])]})]});
            var Q6;
            Q6=makeQuery(id+"F6.boolean.opBoolean","INTERSECT",EDGE,{"disambiguationData":[OD(0.0)],"derivedFrom":[makeQuery(id+"F2.opExtrude","SWEPT_FACE",FACE,{"disambiguationData":[OSD([sQuery(id+"F1.wireOp",EDGE,"E11")])]}),makeQuery(id+"F6.opExtrude","SWEPT_FACE",FACE,{"disambiguationData":[OSD([sQuery(id+"F5.wireOp",EDGE,"E28")])]})]});
            var Q7;
            Q7=makeQuery(id+"F6.boolean.opBoolean","INTERSECT",EDGE,{"disambiguationData":[OD(1.0)],"derivedFrom":[makeQuery(id+"F2.opExtrude","SWEPT_FACE",FACE,{"disambiguationData":[OSD([sQuery(id+"F1.wireOp",EDGE,"E11")])]}),makeQuery(id+"F6.opExtrude","SWEPT_FACE",FACE,{"disambiguationData":[OSD([sQuery(id+"F5.wireOp",EDGE,"E27")])]})]});
            var Q8;
            Q8=makeQuery(id+"F6.boolean.opBoolean","INTERSECT",EDGE,{"disambiguationData":[OD(0.0)],"derivedFrom":[makeQuery(id+"F2.opExtrude","SWEPT_FACE",FACE,{"disambiguationData":[OSD([sQuery(id+"F1.wireOp",EDGE,"E11")])]}),makeQuery(id+"F6.opExtrude","SWEPT_FACE",FACE,{"disambiguationData":[OSD([sQuery(id+"F5.wireOp",EDGE,"E27")])]})]});
            var Q9;
            Q9=makeQuery(id+"F6.boolean.opBoolean","INTERSECT",EDGE,{"disambiguationData":[OD(1.0)],"derivedFrom":[makeQuery(id+"F2.opExtrude","SWEPT_FACE",FACE,{"disambiguationData":[OSD([sQuery(id+"F1.wireOp",EDGE,"E11")])]}),makeQuery(id+"F6.opExtrude","SWEPT_FACE",FACE,{"disambiguationData":[OSD([sQuery(id+"F5.wireOp",EDGE,"E26")])]})]});
            var Q10;
            Q10=makeQuery(id+"F6.boolean.opBoolean","INTERSECT",EDGE,{"disambiguationData":[OD(0.0)],"derivedFrom":[makeQuery(id+"F2.opExtrude","SWEPT_FACE",FACE,{"disambiguationData":[OSD([sQuery(id+"F1.wireOp",EDGE,"E11")])]}),makeQuery(id+"F6.opExtrude","SWEPT_FACE",FACE,{"disambiguationData":[OSD([sQuery(id+"F5.wireOp",EDGE,"E26")])]})]});
            var Q11;
            Q11=makeQuery(id+"F6.boolean.opBoolean","INTERSECT",EDGE,{"disambiguationData":[OD(0.0)],"derivedFrom":[makeQuery(id+"F2.opExtrude","SWEPT_FACE",FACE,{"disambiguationData":[OSD([sQuery(id+"F1.wireOp",EDGE,"E11")])]}),makeQuery(id+"F6.opExtrude","SWEPT_FACE",FACE,{"disambiguationData":[OSD([sQuery(id+"F5.wireOp",EDGE,"E25")])]})]});
            fillet(context, id + "F8", {"entities" : qUnion([Q0, Q1, Q2, Q3, Q4, Q5, Q6, Q7, Q8, Q9, Q10, Q11]), "radius" : 5 * mm, "tangentPropagation" : true, "allowEdgeOverflow" : false});
        }
        {
            var Q0;
            {var subQ0=sQuery(id+"F5.wireOp",EDGE,"E31");var subQ1=sQuery(id+"F5.wireOp",EDGE,"E13");var subQ2=makeQuery(id+"F5.imprint","INTERSECT",VERTEX,{"disambiguationData":[OD(0.0)],"derivedFrom":[subQ1,subQ0]});Q0=makeQuery(id+"F5.imprint","IMPRINT",FACE,{"disambiguationData":[TD([[makeQuery(id+"F5.imprint","IMPRINT",EDGE,{"disambiguationData":[TD([[subQ2,-1.0]])],"derivedFrom":subQ1}),-1.0]])]});}
            var Q1;
            {var subQ0=sQuery(id+"F5.wireOp",EDGE,"E31");var subQ1=sQuery(id+"F5.wireOp",EDGE,"E13");var subQ2=makeQuery(id+"F5.imprint","INTERSECT",VERTEX,{"disambiguationData":[OD(0.0)],"derivedFrom":[subQ1,subQ0]});Q1=makeQuery(id+"F5.imprint","IMPRINT",FACE,{"disambiguationData":[TD([[makeQuery(id+"F5.imprint","IMPRINT",EDGE,{"disambiguationData":[TD([[subQ2,-1.0]])],"derivedFrom":subQ1}),1.0]])]});}
            var Q2;
            {var subQ0=sQuery(id+"F5.wireOp",EDGE,"E32");var subQ1=sQuery(id+"F5.wireOp",EDGE,"E13");var subQ2=makeQuery(id+"F5.imprint","INTERSECT",VERTEX,{"disambiguationData":[OD(0.0)],"derivedFrom":[subQ1,subQ0]});Q2=makeQuery(id+"F5.imprint","IMPRINT",FACE,{"disambiguationData":[TD([[makeQuery(id+"F5.imprint","IMPRINT",EDGE,{"disambiguationData":[TD([[subQ2,-1.0]])],"derivedFrom":subQ1}),-1.0]])]});}
            var Q3;
            {var subQ0=sQuery(id+"F5.wireOp",EDGE,"E32");var subQ1=sQuery(id+"F5.wireOp",EDGE,"E13");var subQ2=makeQuery(id+"F5.imprint","INTERSECT",VERTEX,{"disambiguationData":[OD(0.0)],"derivedFrom":[subQ1,subQ0]});Q3=makeQuery(id+"F5.imprint","IMPRINT",FACE,{"disambiguationData":[TD([[makeQuery(id+"F5.imprint","IMPRINT",EDGE,{"disambiguationData":[TD([[subQ2,-1.0]])],"derivedFrom":subQ1}),1.0]])]});}
            var Q4;
            {var subQ0=sQuery(id+"F5.wireOp",EDGE,"E33");var subQ1=sQuery(id+"F5.wireOp",EDGE,"E13");var subQ2=makeQuery(id+"F5.imprint","INTERSECT",VERTEX,{"disambiguationData":[OD(0.0)],"derivedFrom":[subQ1,subQ0]});Q4=makeQuery(id+"F5.imprint","IMPRINT",FACE,{"disambiguationData":[TD([[makeQuery(id+"F5.imprint","IMPRINT",EDGE,{"disambiguationData":[TD([[subQ2,-1.0]])],"derivedFrom":subQ1}),1.0]])]});}
            var Q5;
            {var subQ0=sQuery(id+"F5.wireOp",EDGE,"E33");var subQ1=sQuery(id+"F5.wireOp",EDGE,"E13");var subQ2=makeQuery(id+"F5.imprint","INTERSECT",VERTEX,{"disambiguationData":[OD(0.0)],"derivedFrom":[subQ1,subQ0]});Q5=makeQuery(id+"F5.imprint","IMPRINT",FACE,{"disambiguationData":[TD([[makeQuery(id+"F5.imprint","IMPRINT",EDGE,{"disambiguationData":[TD([[subQ2,-1.0]])],"derivedFrom":subQ1}),-1.0]])]});}
            var Q6;
            {var subQ0=sQuery(id+"F5.wireOp",EDGE,"E34");var subQ1=sQuery(id+"F5.wireOp",EDGE,"E13");var subQ2=makeQuery(id+"F5.imprint","INTERSECT",VERTEX,{"disambiguationData":[OD(0.0)],"derivedFrom":[subQ1,subQ0]});Q6=makeQuery(id+"F5.imprint","IMPRINT",FACE,{"disambiguationData":[TD([[makeQuery(id+"F5.imprint","IMPRINT",EDGE,{"disambiguationData":[TD([[subQ2,-1.0]])],"derivedFrom":subQ1}),1.0]])]});}
            var Q7;
            {var subQ0=sQuery(id+"F5.wireOp",EDGE,"E34");var subQ1=sQuery(id+"F5.wireOp",EDGE,"E13");var subQ2=makeQuery(id+"F5.imprint","INTERSECT",VERTEX,{"disambiguationData":[OD(0.0)],"derivedFrom":[subQ1,subQ0]});Q7=makeQuery(id+"F5.imprint","IMPRINT",FACE,{"disambiguationData":[TD([[makeQuery(id+"F5.imprint","IMPRINT",EDGE,{"disambiguationData":[TD([[subQ2,-1.0]])],"derivedFrom":subQ1}),-1.0]])]});}
            var Q8;
            {var subQ1=sQuery(id+"F5.wireOp",EDGE,"E36.bottom");Q8=makeQuery(id+"F5.imprint","IMPRINT",FACE,{"disambiguationData":[TD([[makeQuery(id+"F5.imprint","IMPRINT",EDGE,{"derivedFrom":subQ1}),-1.0]])]});}
            var Q9;
            {var subQ0=sQuery(id+"F5.wireOp",EDGE,"E36.top");var subQ1=sQuery(id+"F5.wireOp",EDGE,"E13");var subQ2=makeQuery(id+"F5.imprint","INTERSECT",VERTEX,{"derivedFrom":[subQ1,subQ0]});Q9=makeQuery(id+"F5.imprint","IMPRINT",FACE,{"disambiguationData":[TD([[makeQuery(id+"F5.imprint","IMPRINT",EDGE,{"disambiguationData":[TD([[subQ2,-1.0]])],"derivedFrom":subQ1}),1.0]])]});}
            var Q10;
            {var subQ0=sQuery(id+"F5.wireOp",EDGE,"E35");var subQ1=sQuery(id+"F5.wireOp",EDGE,"E13");var subQ2=makeQuery(id+"F5.imprint","INTERSECT",VERTEX,{"disambiguationData":[OD(0.0)],"derivedFrom":[subQ1,subQ0]});Q10=makeQuery(id+"F5.imprint","IMPRINT",FACE,{"disambiguationData":[TD([[makeQuery(id+"F5.imprint","IMPRINT",EDGE,{"disambiguationData":[TD([[subQ2,-1.0]])],"derivedFrom":subQ1}),-1.0]])]});}
            var Q11;
            {var subQ0=sQuery(id+"F5.wireOp",EDGE,"E35");var subQ1=sQuery(id+"F5.wireOp",EDGE,"E13");var subQ2=makeQuery(id+"F5.imprint","INTERSECT",VERTEX,{"disambiguationData":[OD(0.0)],"derivedFrom":[subQ1,subQ0]});Q11=makeQuery(id+"F5.imprint","IMPRINT",FACE,{"disambiguationData":[TD([[makeQuery(id+"F5.imprint","IMPRINT",EDGE,{"disambiguationData":[TD([[subQ2,-1.0]])],"derivedFrom":subQ1}),1.0]])]});}
            extrude(context, id + "F9", {"entities" : qUnion([Q0, Q1, Q2, Q3, Q4, Q5, Q6, Q7, Q8, Q9, Q10, Q11]), "operationType" : NewBodyOperationType.ADD, "depth" : 8 * mm, "offsetDistance" : 25 * mm});
        }
        {
            var Q0;
            Q0=makeQuery(id+"F9.opExtrude","CAP_EDGE",EDGE,{"disambiguationData":[OSD([sQuery(id+"F5.wireOp",EDGE,"E35")])],"isStart":false});
            var Q1;
            Q1=makeQuery(id+"F9.opExtrude","CAP_FACE",FACE,{"disambiguationData":[OSD([sQuery(id+"F5.wireOp",EDGE,"E31")])],"isStart":false});
            var Q2;
            Q2=makeQuery(id+"F9.opExtrude","CAP_FACE",FACE,{"disambiguationData":[OSD([sQuery(id+"F5.wireOp",EDGE,"E32")])],"isStart":false});
            var Q3;
            Q3=makeQuery(id+"F9.opExtrude","CAP_FACE",FACE,{"disambiguationData":[OSD([sQuery(id+"F5.wireOp",EDGE,"E33")])],"isStart":false});
            var Q4;
            Q4=makeQuery(id+"F9.opExtrude","CAP_FACE",FACE,{"disambiguationData":[OSD([sQuery(id+"F5.wireOp",EDGE,"E34")])],"isStart":false});
            var Q5;
            Q5=makeQuery(id+"F9.opExtrude","CAP_EDGE",EDGE,{"disambiguationData":[OSD([sQuery(id+"F5.wireOp",EDGE,"E36.left")])],"isStart":false});
            var Q6;
            Q6=makeQuery(id+"F9.opExtrude","CAP_EDGE",EDGE,{"disambiguationData":[OSD([sQuery(id+"F5.wireOp",EDGE,"E36.right")])],"isStart":false});
            var Q7;
            Q7=makeQuery(id+"F9.opExtrude","CAP_EDGE",EDGE,{"disambiguationData":[OSD([sQuery(id+"F5.wireOp",EDGE,"E36.bottom")])],"isStart":false});
            var Q8;
            Q8=makeQuery(id+"F9.opExtrude","CAP_EDGE",EDGE,{"disambiguationData":[OSD([sQuery(id+"F5.wireOp",EDGE,"E36.top")])],"isStart":false});
            fillet(context, id + "F10", {"entities" : qUnion([Q0, Q1, Q2, Q3, Q4, Q5, Q6, Q7, Q8]), "radius" : .45 * mm, "tangentPropagation" : true, "allowEdgeOverflow" : false});
        }
        {
            var Q0;
            {var subQ0=sQuery(id+"F5.wireOp",EDGE,"E35");var subQ1=sQuery(id+"F5.wireOp",EDGE,"E13");var subQ2=makeQuery(id+"F5.imprint","INTERSECT",VERTEX,{"disambiguationData":[OD(0.0)],"derivedFrom":[subQ1,subQ0]});Q0=makeQuery(id+"F5.imprint","IMPRINT",FACE,{"disambiguationData":[TD([[makeQuery(id+"F5.imprint","IMPRINT",EDGE,{"disambiguationData":[TD([[subQ2,-1.0]])],"derivedFrom":subQ1}),-1.0]])]});}
            var Q1;
            {var subQ0=sQuery(id+"F5.wireOp",EDGE,"E35");var subQ1=sQuery(id+"F5.wireOp",EDGE,"E13");var subQ2=makeQuery(id+"F5.imprint","INTERSECT",VERTEX,{"disambiguationData":[OD(0.0)],"derivedFrom":[subQ1,subQ0]});Q1=makeQuery(id+"F5.imprint","IMPRINT",FACE,{"disambiguationData":[TD([[makeQuery(id+"F5.imprint","IMPRINT",EDGE,{"disambiguationData":[TD([[subQ2,-1.0]])],"derivedFrom":subQ1}),1.0]])]});}
            var Q2;
            {var subQ1=sQuery(id+"F5.wireOp",EDGE,"E36.bottom");Q2=makeQuery(id+"F5.imprint","IMPRINT",FACE,{"disambiguationData":[TD([[makeQuery(id+"F5.imprint","IMPRINT",EDGE,{"derivedFrom":subQ1}),-1.0]])]});}
            var Q3;
            {var subQ0=sQuery(id+"F5.wireOp",EDGE,"E36.top");var subQ1=sQuery(id+"F5.wireOp",EDGE,"E13");var subQ2=makeQuery(id+"F5.imprint","INTERSECT",VERTEX,{"derivedFrom":[subQ1,subQ0]});Q3=makeQuery(id+"F5.imprint","IMPRINT",FACE,{"disambiguationData":[TD([[makeQuery(id+"F5.imprint","IMPRINT",EDGE,{"disambiguationData":[TD([[subQ2,-1.0]])],"derivedFrom":subQ1}),1.0]])]});}
            var Q4;
            {var subQ0=sQuery(id+"F5.wireOp",EDGE,"E34");var subQ1=sQuery(id+"F5.wireOp",EDGE,"E13");var subQ2=makeQuery(id+"F5.imprint","INTERSECT",VERTEX,{"disambiguationData":[OD(0.0)],"derivedFrom":[subQ1,subQ0]});Q4=makeQuery(id+"F5.imprint","IMPRINT",FACE,{"disambiguationData":[TD([[makeQuery(id+"F5.imprint","IMPRINT",EDGE,{"disambiguationData":[TD([[subQ2,-1.0]])],"derivedFrom":subQ1}),1.0]])]});}
            var Q5;
            {var subQ0=sQuery(id+"F5.wireOp",EDGE,"E34");var subQ1=sQuery(id+"F5.wireOp",EDGE,"E13");var subQ2=makeQuery(id+"F5.imprint","INTERSECT",VERTEX,{"disambiguationData":[OD(0.0)],"derivedFrom":[subQ1,subQ0]});Q5=makeQuery(id+"F5.imprint","IMPRINT",FACE,{"disambiguationData":[TD([[makeQuery(id+"F5.imprint","IMPRINT",EDGE,{"disambiguationData":[TD([[subQ2,-1.0]])],"derivedFrom":subQ1}),-1.0]])]});}
            var Q6;
            {var subQ0=sQuery(id+"F5.wireOp",EDGE,"E33");var subQ1=sQuery(id+"F5.wireOp",EDGE,"E13");var subQ2=makeQuery(id+"F5.imprint","INTERSECT",VERTEX,{"disambiguationData":[OD(0.0)],"derivedFrom":[subQ1,subQ0]});Q6=makeQuery(id+"F5.imprint","IMPRINT",FACE,{"disambiguationData":[TD([[makeQuery(id+"F5.imprint","IMPRINT",EDGE,{"disambiguationData":[TD([[subQ2,-1.0]])],"derivedFrom":subQ1}),1.0]])]});}
            var Q7;
            {var subQ0=sQuery(id+"F5.wireOp",EDGE,"E33");var subQ1=sQuery(id+"F5.wireOp",EDGE,"E13");var subQ2=makeQuery(id+"F5.imprint","INTERSECT",VERTEX,{"disambiguationData":[OD(0.0)],"derivedFrom":[subQ1,subQ0]});Q7=makeQuery(id+"F5.imprint","IMPRINT",FACE,{"disambiguationData":[TD([[makeQuery(id+"F5.imprint","IMPRINT",EDGE,{"disambiguationData":[TD([[subQ2,-1.0]])],"derivedFrom":subQ1}),-1.0]])]});}
            var Q8;
            {var subQ0=sQuery(id+"F5.wireOp",EDGE,"E32");var subQ1=sQuery(id+"F5.wireOp",EDGE,"E13");var subQ2=makeQuery(id+"F5.imprint","INTERSECT",VERTEX,{"disambiguationData":[OD(0.0)],"derivedFrom":[subQ1,subQ0]});Q8=makeQuery(id+"F5.imprint","IMPRINT",FACE,{"disambiguationData":[TD([[makeQuery(id+"F5.imprint","IMPRINT",EDGE,{"disambiguationData":[TD([[subQ2,-1.0]])],"derivedFrom":subQ1}),1.0]])]});}
            var Q9;
            {var subQ0=sQuery(id+"F5.wireOp",EDGE,"E32");var subQ1=sQuery(id+"F5.wireOp",EDGE,"E13");var subQ2=makeQuery(id+"F5.imprint","INTERSECT",VERTEX,{"disambiguationData":[OD(0.0)],"derivedFrom":[subQ1,subQ0]});Q9=makeQuery(id+"F5.imprint","IMPRINT",FACE,{"disambiguationData":[TD([[makeQuery(id+"F5.imprint","IMPRINT",EDGE,{"disambiguationData":[TD([[subQ2,-1.0]])],"derivedFrom":subQ1}),-1.0]])]});}
            var Q10;
            {var subQ0=sQuery(id+"F5.wireOp",EDGE,"E31");var subQ1=sQuery(id+"F5.wireOp",EDGE,"E13");var subQ2=makeQuery(id+"F5.imprint","INTERSECT",VERTEX,{"disambiguationData":[OD(0.0)],"derivedFrom":[subQ1,subQ0]});Q10=makeQuery(id+"F5.imprint","IMPRINT",FACE,{"disambiguationData":[TD([[makeQuery(id+"F5.imprint","IMPRINT",EDGE,{"disambiguationData":[TD([[subQ2,-1.0]])],"derivedFrom":subQ1}),-1.0]])]});}
            var Q11;
            {var subQ0=sQuery(id+"F5.wireOp",EDGE,"E31");var subQ1=sQuery(id+"F5.wireOp",EDGE,"E13");var subQ2=makeQuery(id+"F5.imprint","INTERSECT",VERTEX,{"disambiguationData":[OD(0.0)],"derivedFrom":[subQ1,subQ0]});Q11=makeQuery(id+"F5.imprint","IMPRINT",FACE,{"disambiguationData":[TD([[makeQuery(id+"F5.imprint","IMPRINT",EDGE,{"disambiguationData":[TD([[subQ2,-1.0]])],"derivedFrom":subQ1}),1.0]])]});}
            extrude(context, id + "F11", {"entities" : qUnion([Q0, Q1, Q2, Q3, Q4, Q5, Q6, Q7, Q8, Q9, Q10, Q11]), "operationType" : NewBodyOperationType.REMOVE, "depth" : 1.8 * mm, "offsetDistance" : 25 * mm});
        }
        {
            var Q0;
            Q0=qCreatedBy(makeId("Top.planeOp"),FACE);
            var sketch = newSketch(context, id + "F12", { "sketchPlane" : qUnion([Q0])});
            skCircle(sketch, "E37", {"center": v(0, 0) * mm, "radius": 13.47 * mm});
            skSolve(sketch);
        }
        {
            var Q0;
            {var subQ0=sQuery(id+"F0.wireOp",EDGE,"E8.right");var subQ1=sQuery(id+"F0.wireOp",EDGE,"E1.0");var subQ2=makeQuery(id+"F0.imprint","INTERSECT",VERTEX,{"disambiguationData":[OD(1.0)],"derivedFrom":[subQ1,subQ0]});Q0=makeQuery(id+"F0.imprint","IMPRINT",FACE,{"disambiguationData":[TD([[makeQuery(id+"F0.imprint","IMPRINT",EDGE,{"disambiguationData":[TD([[subQ2,-1.0]])],"derivedFrom":subQ1}),1.0]])]});}
            var Q1;
            {var subQ0=sQuery(id+"F0.wireOp",EDGE,"E3.right");var subQ1=sQuery(id+"F0.wireOp",EDGE,"E1.0");var subQ2=makeQuery(id+"F0.imprint","INTERSECT",VERTEX,{"disambiguationData":[OD(0.0)],"derivedFrom":[subQ1,subQ0]});Q1=makeQuery(id+"F0.imprint","IMPRINT",FACE,{"disambiguationData":[TD([[makeQuery(id+"F0.imprint","IMPRINT",EDGE,{"disambiguationData":[TD([[subQ2,1.0]])],"derivedFrom":subQ1}),1.0]])]});}
            var Q2;
            {var subQ0=sQuery(id+"F0.wireOp",EDGE,"E3.left");var subQ1=sQuery(id+"F0.wireOp",EDGE,"E1.0");var subQ2=makeQuery(id+"F0.imprint","INTERSECT",VERTEX,{"disambiguationData":[OD(0.0)],"derivedFrom":[subQ1,subQ0]});Q2=makeQuery(id+"F0.imprint","IMPRINT",FACE,{"disambiguationData":[TD([[makeQuery(id+"F0.imprint","IMPRINT",EDGE,{"disambiguationData":[TD([[subQ2,-1.0]])],"derivedFrom":subQ1}),1.0]])]});}
            extrude(context, id + "F13", {"entities" : qUnion([Q0, Q1, Q2]), "operationType" : NewBodyOperationType.REMOVE, "depth" : 1 * mm, "offsetDistance" : 25 * mm});
        }
        {
            var Q0;
            Q0=makeQuery(id+"F12.imprint","IMPRINT",FACE,{"disambiguationData":[TD([[makeQuery(id+"F12.imprint","IMPRINT",EDGE,{"derivedFrom":sQuery(id+"F12.wireOp",EDGE,"E37")}),1.0]])]});
            extrude(context, id + "F14", {"entities" : qUnion([Q0]), "operationType" : NewBodyOperationType.REMOVE, "depth" : 1 * mm, "offsetDistance" : 25 * mm});
        }
        {
            var Q0;
            Q0=makeQuery(id+"F13.boolean.opBoolean","COPY",EDGE,{"derivedFrom":makeQuery(id+"F13.opExtrude","SWEPT_EDGE",EDGE,{"disambiguationData":[OSD([sQuery(id+"F0.wireOp",EDGE,"E1.0"),sQuery(id+"F0.wireOp",EDGE,"E2.right")])]})});
            var Q1;
            Q1=makeQuery(id+"F13.boolean.opBoolean","COPY",EDGE,{"derivedFrom":makeQuery(id+"F13.opExtrude","SWEPT_EDGE",EDGE,{"disambiguationData":[OSD([sQuery(id+"F0.wireOp",EDGE,"E1.0"),sQuery(id+"F0.wireOp",EDGE,"E3.right")])]})});
            var Q2;
            Q2=makeQuery(id+"F13.boolean.opBoolean","COPY",EDGE,{"derivedFrom":makeQuery(id+"F13.opExtrude","SWEPT_EDGE",EDGE,{"disambiguationData":[OSD([sQuery(id+"F0.wireOp",EDGE,"E1.0"),sQuery(id+"F0.wireOp",EDGE,"E3.left")])]})});
            var Q3;
            Q3=makeQuery(id+"F13.boolean.opBoolean","COPY",EDGE,{"derivedFrom":makeQuery(id+"F13.opExtrude","SWEPT_EDGE",EDGE,{"disambiguationData":[OSD([sQuery(id+"F0.wireOp",EDGE,"E1.0"),sQuery(id+"F0.wireOp",EDGE,"E6.bottom")])]})});
            var Q4;
            Q4=makeQuery(id+"F13.boolean.opBoolean","COPY",EDGE,{"derivedFrom":makeQuery(id+"F13.opExtrude","SWEPT_EDGE",EDGE,{"disambiguationData":[OSD([sQuery(id+"F0.wireOp",EDGE,"E1.0"),sQuery(id+"F0.wireOp",EDGE,"E9.left")])]})});
            var Q5;
            Q5=makeQuery(id+"F13.boolean.opBoolean","COPY",EDGE,{"derivedFrom":makeQuery(id+"F13.opExtrude","SWEPT_EDGE",EDGE,{"disambiguationData":[OSD([sQuery(id+"F0.wireOp",EDGE,"E1.0"),sQuery(id+"F0.wireOp",EDGE,"E8.right")])]})});
            fillet(context, id + "F15", {"entities" : qUnion([Q0, Q1, Q2, Q3, Q4, Q5]), "radius" : 1 * mm, "tangentPropagation" : true, "allowEdgeOverflow" : false});
        }
    });
